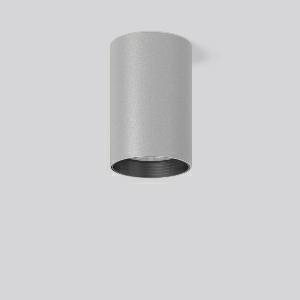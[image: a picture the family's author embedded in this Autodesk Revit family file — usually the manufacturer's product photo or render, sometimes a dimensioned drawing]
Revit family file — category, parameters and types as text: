
# Revit family: heledon_maxi_a_931221_004_1_76_2d8d
name_source: partatom
category: Lighting Fixtures
units: mm (PartAtom-declared; Revit-internal decimal feet)

## family parameters
Cut with Voids When Loaded = No
Host = Face
Light Source = No
Part Type = Normal
Room Calculation Point = No
Round Connector Dimension = Use Diameter
Shared = No

## types (1)
- HELEDON maxi A (1 x LED Modul 940, 2850 lm, 4000)
    Apparent Load = 25 VA
    Approval mark = CE
    CIE Flux Codes = 96 100 100 100 100
    Color Rendering = 92
    Color Temperature = 4000
    Default Elevation = 1800 mm
    Description = Series: HELEDON maxi
Cylindrical surface-mounted downlight. Housing: die-cast aluminium, powder-coated. Internal ceiling frame polycarbonate with bayonet mounting. Black plastic ring and recessed LED to prevent glare from the side. Optical assembly with lens made of plastic (polycarbonate) for the best homogeneous light distribution - can be changed without tools. Best colour rendering index Ra>90. Suitable for Ceiling mounting. Easy installation with a separate ceiling frame with bayonet mounting and plug connection. Driver integrated. Connected via plug-in connector. High quality converter without flickering and stroboscopic effect. The following accessories can be mounted without use of tools: interchangeable lenses, decorative glasses, honeycomb louvre, clear and frosted diffusers, white interchangeable plastic ring. 
Colour: silver
Diameter: 123 mm
Height: 183 mm
Lamp: LED
Socket: without socket
Colour temperature: 4000K
Colour rendering index (CRI): 92
System power: 25 W
Rated luminous flux: 2850 lm
Luminous efficiency: 114 lm/W
Control gear: Converter, dimmable, DALI
Protection class: I
Type of protection: IP 20
    Height = 183 mm
    Lamp = 1 x LED Modul 940
    Lamp Light Flux = 2850 lm
    Lamp count = 1
    Length = 123 mm
    Lifetime = 50000 h
    Luminous efficacy = 114 lm/W
    Manufacturer = RZB
    ModVariant = No
    Model = 931221.004.1.76
    Mounting Place = Ceiling
    Mounting Type = Surface mounted
    Number of Poles = 1
    OnlyDefault = Yes
    Power Factor = 1
    Product Name = HELEDON maxi A
    Product group = Surface mounted downlights
    ProductGroupID = 302
    Protection Class = Protection class I
    Protection Degree = IP 20
    RLX_Detail_Level = 1
    RLX_Emergency_Light_Flux = 0 lm
    RLX_Emergency_Type = 0
    RLX_Emergency_Type_DB = No
    RlxData = <blob elided: 99045 chars, md5=92772559>
    Socket = socket
    Standby Power = 0 W
    System Light Flux = 2850 lm
    System Power = 25 W
    Type Comments = Product without accessories
    Type Image = 931193.004.jpg
    URL = http://relux.com
    VarID = ---
    Voltage = 230 V
    Voltage Range = 220-240 V
    Weight = 0.00 kg
    Width = 0 mm  [stored 0 ft]

note: [stored X ft] marks values corroborated as IEEE doubles in the binary element streams (Revit-internal decimal feet)

## geometry (parser evidence)
native form markers: Blend x4, Sweep x11
no freeform markers — native parametric forms only
